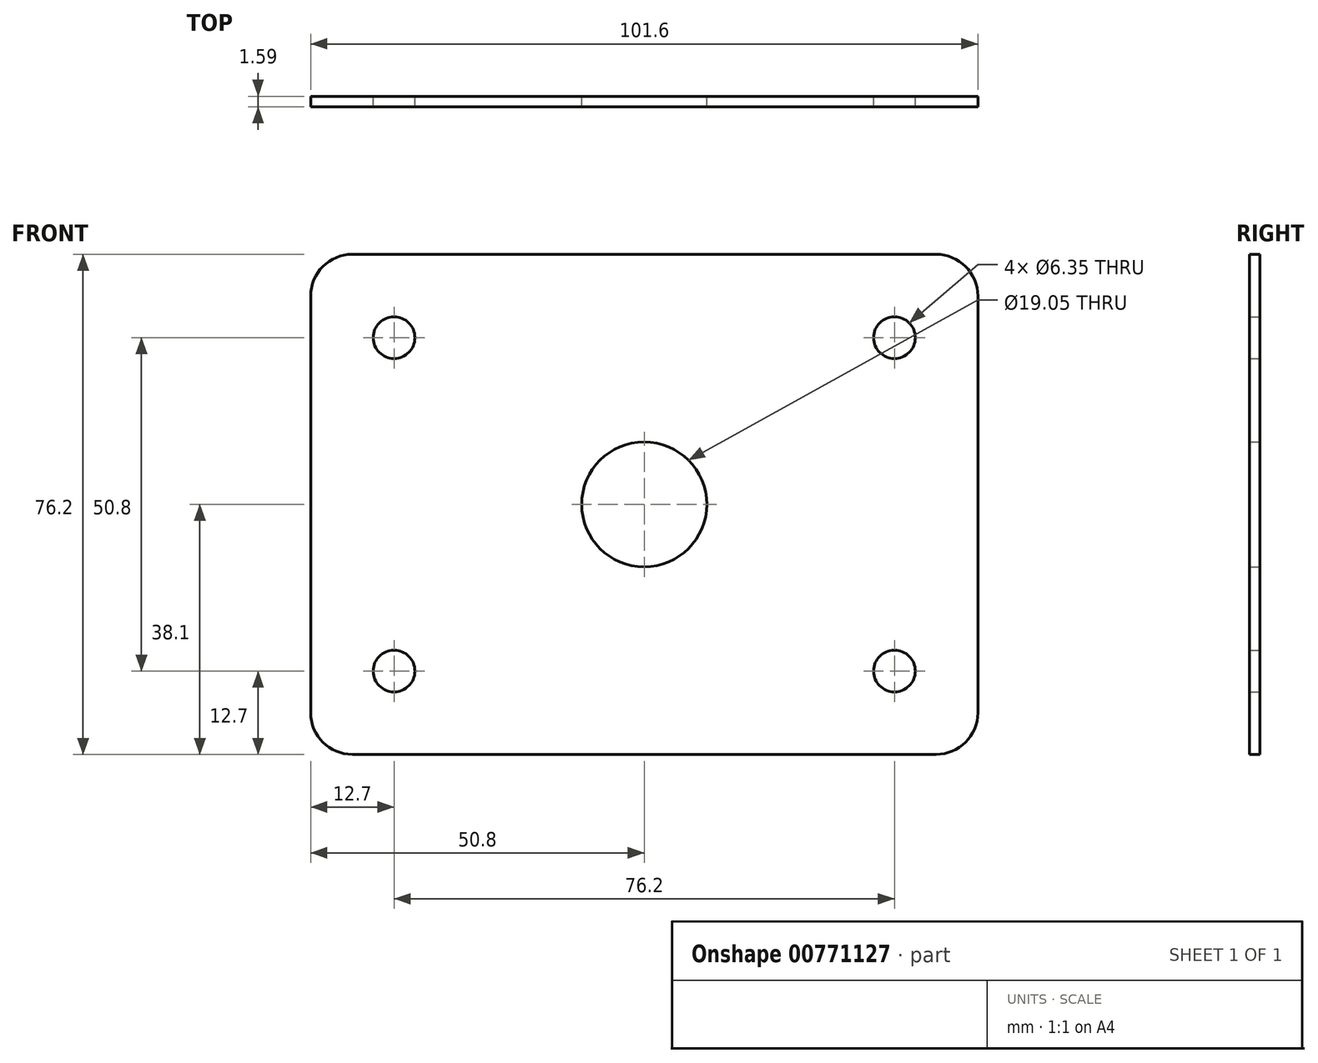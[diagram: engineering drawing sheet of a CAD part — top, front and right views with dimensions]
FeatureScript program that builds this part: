
annotation { "Feature Type Name" : "Feature", "Feature Type Description" : "" }
export const myFeature = defineFeature(function(context is Context, id is Id, definition is map)
    precondition{}
    {
        {
            var Q0;
            Q0=qCreatedBy(makeId("Front.planeOp"),FACE);
            var sketch = newSketch(context, id + "F0", { "sketchPlane" : qUnion([Q0])});
            skLineSegment(sketch, "E0.bottom", {"start": v(50.8, 38.1) * mm, "end": v(-50.8, 38.1) * mm});
            skLineSegment(sketch, "E0.top", {"start": v(50.8, -38.1) * mm, "end": v(-50.8, -38.1) * mm});
            skLineSegment(sketch, "E0.left", {"start": v(50.8, 38.1) * mm, "end": v(50.8, -38.1) * mm});
            skLineSegment(sketch, "E0.right", {"start": v(-50.8, 38.1) * mm, "end": v(-50.8, -38.1) * mm});
            skPoint(sketch, "E0.middle", {"position": v(0, 0) * mm});
            skCircle(sketch, "E1", {"center": v(0, 0) * mm, "radius": 9.53 * mm});
            skCircle(sketch, "E2", {"center": v(-38.1, 25.4) * mm, "radius": 3.18 * mm});
            skCircle(sketch, "E3", {"center": v(38.1, 25.4) * mm, "radius": 3.18 * mm});
            skCircle(sketch, "E4", {"center": v(38.1, -25.4) * mm, "radius": 3.18 * mm});
            skCircle(sketch, "E5", {"center": v(-38.1, -25.4) * mm, "radius": 3.18 * mm});
            skSolve(sketch);
        }
        {
            var Q0;
            Q0=makeQuery(id+"F0.imprint","IMPRINT",FACE,{"disambiguationData":[TD([[makeQuery(id+"F0.imprint","IMPRINT",EDGE,{"derivedFrom":sQuery(id+"F0.wireOp",EDGE,"E0.bottom")}),1.0]])]});
            extrude(context, id + "F1", {"entities" : qUnion([Q0]), "depth" : 1.59 * mm, "offsetDistance" : 25.4 * mm});
        }
        {
            var Q0;
            Q0=makeQuery(id+"F1.opExtrude","SWEPT_EDGE",EDGE,{"disambiguationData":[OSD([sQuery(id+"F0.wireOp",EDGE,"E0.bottom"),sQuery(id+"F0.wireOp",EDGE,"E0.left")])]});
            var Q1;
            Q1=makeQuery(id+"F1.opExtrude","SWEPT_EDGE",EDGE,{"disambiguationData":[OSD([sQuery(id+"F0.wireOp",EDGE,"E0.top"),sQuery(id+"F0.wireOp",EDGE,"E0.left")])]});
            var Q2;
            Q2=makeQuery(id+"F1.opExtrude","SWEPT_EDGE",EDGE,{"disambiguationData":[OSD([sQuery(id+"F0.wireOp",EDGE,"E0.top"),sQuery(id+"F0.wireOp",EDGE,"E0.right")])]});
            var Q3;
            Q3=makeQuery(id+"F1.opExtrude","SWEPT_EDGE",EDGE,{"disambiguationData":[OSD([sQuery(id+"F0.wireOp",EDGE,"E0.bottom"),sQuery(id+"F0.wireOp",EDGE,"E0.right")])]});
            fillet(context, id + "F2", {"entities" : qUnion([Q0, Q1, Q2, Q3]), "radius" : 6.35 * mm, "tangentPropagation" : true, "allowEdgeOverflow" : false});
        }
    });
